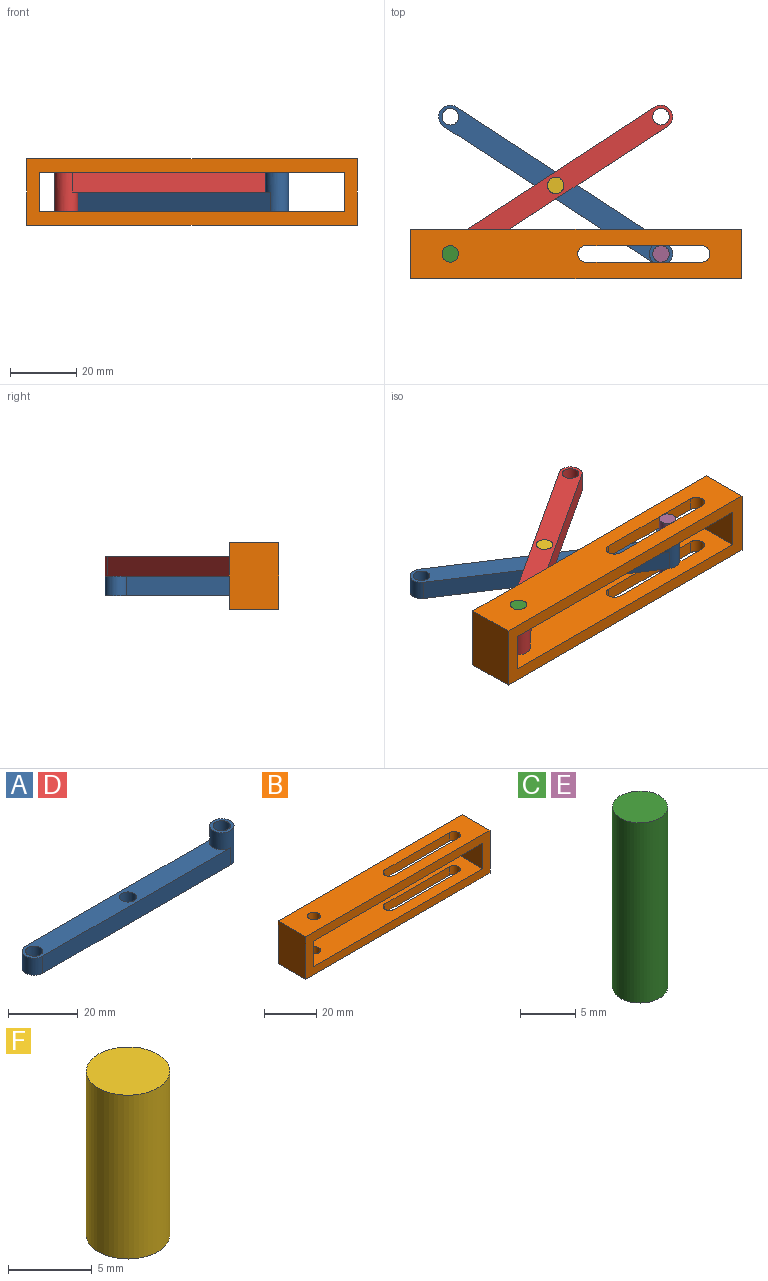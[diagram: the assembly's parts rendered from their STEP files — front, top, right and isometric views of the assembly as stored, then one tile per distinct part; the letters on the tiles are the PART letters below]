
ASSEMBLY  parts=6 mates=6
PART A: 10 faces, bbox 83x7x12 mm
  f0: cylinder r=3.5mm len=12mm, axis (0,0,-1), area 197.9mm2, adj f1,f6,f7,f8,f9
  f1: plane 76x6mm, normal (0,1,0), area 456mm2, adj f0,f2,f7,f8
  f2: cylinder r=3.5mm len=7mm, axis (0,0,-1), area 66mm2, adj f1,f6,f7,f8
  f3: cylinder r=2.5mm len=12mm, axis (0,0,-1), area 188.5mm2, adj f8,f9
  f4: cylinder r=2.5mm len=6mm, axis (0,0,-1), area 94.2mm2, adj f7,f8
  f5: cylinder r=2.5mm len=6mm, axis (0,0,-1), area 94.2mm2, adj f7,f8
  f6: plane 76x6mm, normal (0,-1,0), area 456mm2, adj f0,f2,f7,f8
  f7: plane 79.5x7mm, normal (0,0,1), area 492.7mm2, adj f0,f1,f2,f4,f5,f6
  f8: plane 83x7mm, normal (0,0,-1), area 511.6mm2, adj f0,f1,f2,f3,f4,f5,f6
  f9: plane 7x7mm, normal (0,0,1), area 18.8mm2, adj f0,f3
PART B: 20 faces, bbox 100x15x20 mm
  f0: cylinder r=2.5mm len=5mm, axis (0,0,-1), area 31.4mm2, adj f1,f4,f15,f18
  f1: plane 35x4mm, normal (0,-1,0), area 140mm2, adj f0,f2,f15,f18
  f2: cylinder r=2.5mm len=5mm, axis (0,0,-1), area 31.4mm2, adj f1,f4,f15,f18
  f3: cylinder r=2.5mm len=5mm, axis (0,0,-1), area 62.8mm2, adj f15,f18
  f4: plane 35x4mm, normal (0,1,0), area 140mm2, adj f0,f2,f15,f18
  f5: plane 100x20mm, normal (0,1,0), area 896mm2, adj f6,f13,f14,f15,f16,f17,f18,f19
  f6: plane 20x15mm, normal (-1,0,0), area 300mm2, adj f5,f7,f14,f15
  f7: plane 100x20mm, normal (0,-1,0), area 896mm2, adj f6,f13,f14,f15,f16,f17,f18,f19
  f8: cylinder r=2.5mm len=5mm, axis (0,0,-1), area 31.4mm2, adj f9,f12,f14,f19
  f9: plane 35x4mm, normal (0,-1,0), area 140mm2, adj f8,f10,f14,f19
  f10: cylinder r=2.5mm len=5mm, axis (0,0,-1), area 31.4mm2, adj f9,f12,f14,f19
  f11: cylinder r=2.5mm len=5mm, axis (0,0,-1), area 62.8mm2, adj f14,f19
  f12: plane 35x4mm, normal (0,1,0), area 140mm2, adj f8,f10,f14,f19
  f13: plane 20x15mm, normal (1,0,0), area 300mm2, adj f5,f7,f14,f15
  f14: plane 100x15mm, normal (0,0,1), area 1285.7mm2, adj f5,f6,f7,f8,f9,f10,f11,f12
  f15: plane 100x15mm, normal (0,0,-1), area 1285.7mm2, adj f0,f1,f2,f3,f4,f5,f6,f7
  f16: plane 15x12mm, normal (-1,0,0), area 180mm2, adj f5,f7,f18,f19
  f17: plane 15x12mm, normal (1,0,0), area 180mm2, adj f5,f7,f18,f19
  f18: plane 92x15mm, normal (0,0,1), area 1165.7mm2, adj f0,f1,f2,f3,f4,f5,f7,f16
  f19: plane 92x15mm, normal (0,0,-1), area 1165.7mm2, adj f5,f7,f8,f9,f10,f11,f12,f16
PART C: 3 faces, bbox 5x5x20 mm
  f0: cylinder r=2.5mm len=20mm, axis (0,0,-1), area 314.2mm2, adj f1,f2
  f1: plane 5x5mm, normal (0,0,1), area 19.6mm2, adj f0
  f2: plane 5x5mm, normal (0,0,-1), area 19.6mm2, adj f0
PART D: same geometry as A
PART E: same geometry as C
PART F: 3 faces, bbox 5x5x12 mm
  f0: cylinder r=2.5mm len=12mm, axis (0,0,-1), area 188.5mm2, adj f1,f2
  f1: plane 5x5mm, normal (0,0,1), area 19.6mm2, adj f0
  f2: plane 5x5mm, normal (0,0,-1), area 19.6mm2, adj f0
PLACE A rot(axis=(0,0,-1),33.1deg) t=(-110.09,-47.86,4)mm
PLACE B at identity fixed
PLACE C t=(-157.4,-66.68,0)mm
PLACE D rot(axis=(0.28,-0.96,0),180deg) t=(-141.02,-47.86,16)mm
PLACE E rot(axis=(0,0,-1),69.3deg) t=(-93.71,-66.68,0)mm
PLACE F rot(axis=(0,0,-1),27.9deg) t=(-125.56,-45.95,4)mm
MATE pin_slot E.f0 <-> B.f2  axis (0,0,1) through (-93.71,-66.68,20)mm
MATE revolute D.f5 <-> F.f0  axis (0,0,1) through (-125.56,-45.95,16)mm
MATE revolute D.f0 <-> C.f0  axis (0,0,1) through (-157.4,-66.68,10)mm
MATE revolute F.f0 <-> A.f5  axis (0,0,-1) through (-125.56,-45.95,4)mm
MATE fastened C.f0 <-> B.f3  axis (0,0,1) through (-157.4,-66.68,20)mm
MATE revolute A.f0 <-> E.f0  axis (0,0,-1) through (-93.71,-66.68,10)mm
